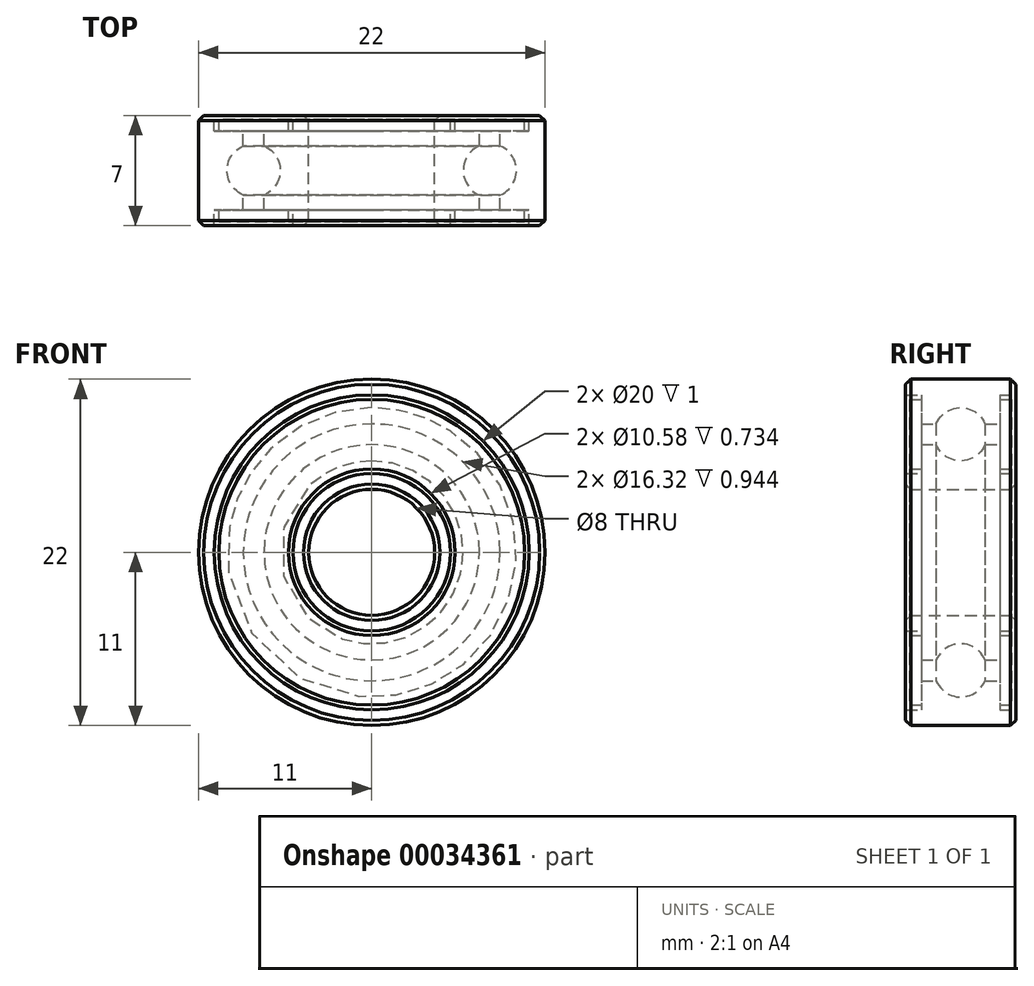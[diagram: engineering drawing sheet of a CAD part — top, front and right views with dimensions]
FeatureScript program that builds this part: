
annotation { "Feature Type Name" : "Feature", "Feature Type Description" : "" }
export const myFeature = defineFeature(function(context is Context, id is Id, definition is map)
    precondition{}
    {
        {
            var Q0;
            Q0=qCreatedBy(makeId("Front.planeOp"),FACE);
            var sketch = newSketch(context, id + "F0", { "sketchPlane" : qUnion([Q0])});
            skCircle(sketch, "E0.0", {"center": v(0, 0) * mm, "radius": 11 * mm});
            skCircle(sketch, "E0.1", {"center": v(0, 0) * mm, "radius": 6.84 * mm});
            skCircle(sketch, "E0.2", {"center": v(0, 0) * mm, "radius": 8.16 * mm});
            skCircle(sketch, "E0.3", {"center": v(0, 0) * mm, "radius": 4 * mm});
            skSolve(sketch);
        }
        {
            var Q0;
            Q0=qCreatedBy(makeId("Right.planeOp"),FACE);
            var sketch = newSketch(context, id + "F1", { "sketchPlane" : qUnion([Q0])});
            skLineSegment(sketch, "E1.0.0", {"start": v(3.5, 11) * mm, "end": v(0, 11) * mm});
            skArc(sketch, "E1.0.4", {"start": v(0, 9.19) * mm, "mid": v(0.93, 8.9) * mm, "end": v(1.56, 8.16) * mm});
            skLineSegment(sketch, "E1.0.5", {"start": v(1.56, 8.16) * mm, "end": v(3.5, 8.16) * mm});
            skLineSegment(sketch, "E1.0.6", {"start": v(3.5, 8.16) * mm, "end": v(3.5, 11) * mm});
            skLineSegment(sketch, "E1.1.3", {"start": v(0, 4) * mm, "end": v(3.5, 4) * mm});
            skLineSegment(sketch, "E1.1.5", {"start": v(3.5, 4) * mm, "end": v(3.5, 6.84) * mm});
            skLineSegment(sketch, "E1.1.6", {"start": v(3.5, 6.84) * mm, "end": v(1.56, 6.84) * mm});
            skArc(sketch, "E1.1.7", {"start": v(1.56, 6.84) * mm, "mid": v(0.93, 6.1) * mm, "end": v(0, 5.81) * mm});
            skLineSegment(sketch, "E2", {"start": v(-5.57, 7.5) * mm, "end": v(5.65, 7.5) * mm, "construction": true});
            skLineSegment(sketch, "E3", {"start": v(0, 11) * mm, "end": v(0, 9.19) * mm});
            skLineSegment(sketch, "E4", {"start": v(0, 5.81) * mm, "end": v(0, 4) * mm});
            skLineSegment(sketch, "E5", {"start": v(0, 12.74) * mm, "end": v(0, 2.66) * mm, "construction": true});
            skLineSegment(sketch, "E6.rect.bottom", {"start": v(3.5, 5) * mm, "end": v(2.5, 5) * mm});
            skLineSegment(sketch, "E6.rect.top", {"start": v(3.5, 10) * mm, "end": v(2.5, 10) * mm});
            skLineSegment(sketch, "E6.rect.right", {"start": v(2.5, 5) * mm, "end": v(2.5, 10) * mm});
            skPoint(sketch, "E6.rect.middle", {"position": v(3.5, 7.5) * mm});
            skLineSegment(sketch, "E7.MirrorCS", {"start": v(-1.56, 8.16) * mm, "end": v(-3.5, 8.16) * mm});
            skLineSegment(sketch, "E8.MirrorCS", {"start": v(0, 4) * mm, "end": v(-3.5, 4) * mm});
            skArc(sketch, "E9.MirrorCS", {"start": v(-1.56, 6.84) * mm, "mid": v(-0.93, 6.1) * mm, "end": v(0, 5.81) * mm});
            skLineSegment(sketch, "E10.MirrorCS", {"start": v(-3.5, 6.84) * mm, "end": v(-1.56, 6.84) * mm});
            skArc(sketch, "E11.MirrorCS", {"start": v(0, 9.19) * mm, "mid": v(-0.93, 8.9) * mm, "end": v(-1.56, 8.16) * mm});
            skLineSegment(sketch, "E12.MirrorCS", {"start": v(-3.5, 8.16) * mm, "end": v(-3.5, 11) * mm});
            skLineSegment(sketch, "E13.MirrorCS", {"start": v(-3.5, 4) * mm, "end": v(-3.5, 6.84) * mm});
            skLineSegment(sketch, "E14.MirrorCS", {"start": v(-3.5, 11) * mm, "end": v(0, 11) * mm});
            skLineSegment(sketch, "E15", {"start": v(3.23, 10) * mm, "end": v(3.23, 5) * mm});
            skLineSegment(sketch, "E16", {"start": v(2.5, 9.7) * mm, "end": v(3.5, 9.7) * mm});
            skLineSegment(sketch, "E17.MirrorCS", {"start": v(2.5, 5.3) * mm, "end": v(3.5, 5.3) * mm});
            skLineSegment(sketch, "E18.MirrorCS", {"start": v(-2.5, 9.7) * mm, "end": v(-3.5, 9.7) * mm});
            skLineSegment(sketch, "E19.MirrorCS", {"start": v(-2.5, 5.3) * mm, "end": v(-3.5, 5.3) * mm});
            skLineSegment(sketch, "E20.MirrorCS", {"start": v(-3.23, 10) * mm, "end": v(-3.23, 5) * mm});
            skLineSegment(sketch, "E21.MirrorCS", {"start": v(-3.5, 10) * mm, "end": v(-2.5, 10) * mm});
            skLineSegment(sketch, "E22.MirrorCS", {"start": v(-2.5, 5) * mm, "end": v(-2.5, 10) * mm});
            skLineSegment(sketch, "E23.MirrorCS", {"start": v(-3.5, 5) * mm, "end": v(-2.5, 5) * mm});
            skSolve(sketch);
        }
        {
            var Q0;
            {var subQ7=sQuery(id+"F1.wireOp",EDGE,"E1.0.0");Q0=makeQuery(id+"F1.imprint","IMPRINT",FACE,{"disambiguationData":[TD([[makeQuery(id+"F1.imprint","IMPRINT",EDGE,{"derivedFrom":subQ7}),1.0]])]});}
            var Q1;
            {var subQ8=sQuery(id+"F1.wireOp",EDGE,"E1.1.3");Q1=makeQuery(id+"F1.imprint","IMPRINT",FACE,{"disambiguationData":[TD([[makeQuery(id+"F1.imprint","IMPRINT",EDGE,{"derivedFrom":subQ8}),1.0]])]});}
            var Q2;
            Q2=makeQuery(id+"F1.imprint","IMPRINT",FACE,{"disambiguationData":[TD([[makeQuery(id+"F1.imprint","IMPRINT",EDGE,{"derivedFrom":sQuery(id+"F1.wireOp",EDGE,"E4")}),-1.0]])]});
            var Q3;
            Q3=makeQuery(id+"F1.imprint","IMPRINT",FACE,{"disambiguationData":[TD([[makeQuery(id+"F1.imprint","IMPRINT",EDGE,{"derivedFrom":sQuery(id+"F1.wireOp",EDGE,"E3")}),-1.0]])]});
            var Q4;
            {var subQ0=sQuery(id+"F1.wireOp",EDGE,"E15");var subQ3=sQuery(id+"F1.wireOp",EDGE,"E1.0.5");var subQ4=makeQuery(id+"F1.imprint","INTERSECT",VERTEX,{"derivedFrom":[subQ3,subQ0]});Q4=makeQuery(id+"F1.imprint","IMPRINT",FACE,{"disambiguationData":[TD([[makeQuery(id+"F1.imprint","IMPRINT",EDGE,{"disambiguationData":[TD([[subQ4,1.0]])],"derivedFrom":subQ3}),1.0]])]});}
            var Q5;
            {var subQ0=sQuery(id+"F1.wireOp",EDGE,"E15");var subQ3=sQuery(id+"F1.wireOp",EDGE,"E1.0.5");var subQ4=makeQuery(id+"F1.imprint","INTERSECT",VERTEX,{"derivedFrom":[subQ3,subQ0]});Q5=makeQuery(id+"F1.imprint","IMPRINT",FACE,{"disambiguationData":[TD([[makeQuery(id+"F1.imprint","IMPRINT",EDGE,{"disambiguationData":[TD([[subQ4,1.0]])],"derivedFrom":subQ3}),-1.0]])]});}
            var Q6;
            {var subQ1=sQuery(id+"F1.wireOp",EDGE,"E15");var subQ5=sQuery(id+"F1.wireOp",EDGE,"E1.1.6");var subQ6=makeQuery(id+"F1.imprint","INTERSECT",VERTEX,{"derivedFrom":[subQ5,subQ1]});Q6=makeQuery(id+"F1.imprint","IMPRINT",FACE,{"disambiguationData":[TD([[makeQuery(id+"F1.imprint","IMPRINT",EDGE,{"disambiguationData":[TD([[subQ6,-1.0]])],"derivedFrom":subQ5}),1.0]])]});}
            var Q7;
            {var subQ1=sQuery(id+"F1.wireOp",EDGE,"E7.MirrorCS");var subQ5=sQuery(id+"F1.wireOp",EDGE,"E20.MirrorCS");var subQ7=makeQuery(id+"F1.imprint","INTERSECT",VERTEX,{"derivedFrom":[subQ1,subQ5]});Q7=makeQuery(id+"F1.imprint","IMPRINT",FACE,{"disambiguationData":[TD([[makeQuery(id+"F1.imprint","IMPRINT",EDGE,{"disambiguationData":[TD([[subQ7,1.0]])],"derivedFrom":subQ1}),-1.0]])]});}
            var Q8;
            {var subQ1=sQuery(id+"F1.wireOp",EDGE,"E10.MirrorCS");var subQ5=sQuery(id+"F1.wireOp",EDGE,"E20.MirrorCS");var subQ7=makeQuery(id+"F1.imprint","INTERSECT",VERTEX,{"derivedFrom":[subQ1,subQ5]});Q8=makeQuery(id+"F1.imprint","IMPRINT",FACE,{"disambiguationData":[TD([[makeQuery(id+"F1.imprint","IMPRINT",EDGE,{"disambiguationData":[TD([[subQ7,-1.0]])],"derivedFrom":subQ1}),-1.0]])]});}
            var Q9;
            {var subQ3=sQuery(id+"F1.wireOp",EDGE,"E7.MirrorCS");var subQ5=sQuery(id+"F1.wireOp",EDGE,"E20.MirrorCS");var subQ7=makeQuery(id+"F1.imprint","INTERSECT",VERTEX,{"derivedFrom":[subQ3,subQ5]});Q9=makeQuery(id+"F1.imprint","IMPRINT",FACE,{"disambiguationData":[TD([[makeQuery(id+"F1.imprint","IMPRINT",EDGE,{"disambiguationData":[TD([[subQ7,1.0]])],"derivedFrom":subQ3}),1.0]])]});}
            var Q10;
            Q10=sQuery(id+"F0.wireOp",EDGE,"E0.0");
            revolve(context, id + "F2", {"entities" : qUnion([Q0, Q1, Q2, Q3, Q4, Q5, Q6, Q7, Q8, Q9]), "axis" : qUnion([Q10]), "revolveType" : RevolveType.FULL});
        }
        {
            var Q0;
            Q0=makeQuery(id+"F2.opRevolve","SWEPT_FACE",FACE,{"disambiguationData":[OSD([sQuery(id+"F1.wireOp",EDGE,"E1.1.3"),sQuery(id+"F1.wireOp",EDGE,"E8.MirrorCS")])]});
            var Q1;
            Q1=makeQuery(id+"F2.opRevolve","SWEPT_FACE",FACE,{"disambiguationData":[OSD([sQuery(id+"F1.wireOp",EDGE,"E1.0.0"),sQuery(id+"F1.wireOp",EDGE,"E14.MirrorCS")])]});
            chamfer(context, id + "F3", {"entities" : qUnion([Q0, Q1]), "width" : .33 * mm, "tangentPropagation" : true});
        }
    });
